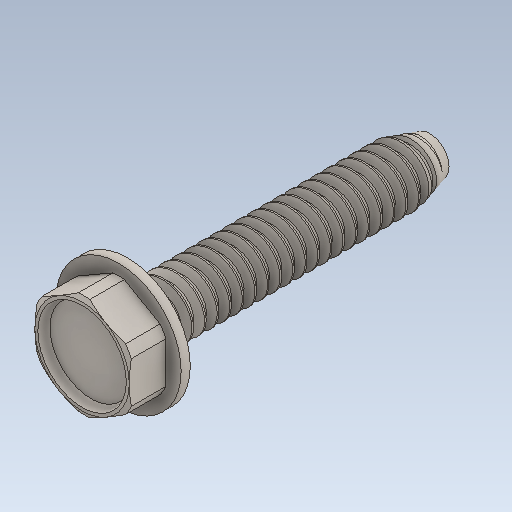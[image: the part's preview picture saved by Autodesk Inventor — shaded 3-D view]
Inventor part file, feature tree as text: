
AUTODESK INVENTOR PART (.ipt)
format: ipt  version: 2020.2 (Build 242310000, 310)  size: 513,536 bytes
history: native  units: in
note: dims shown in document units (in); Inventor stores cm internally (conversion verified against a paired STEP export)
features: chamfer x1
ambient origin geometry x8: Origin, YZ Plane, XZ Plane, XY Plane, X Axis, Y Axis, Z Axis, Center Point
bodies: Solid1 (feature_tree)
feature tree (1):
  chamfer  "Chamfer1"  [1 undecoded]
note: 1 required parameter value undecoded (feature->parameter linkage not recoverable at this tier; creation-order binding heuristic only, values carry confidence <= 0.55)
